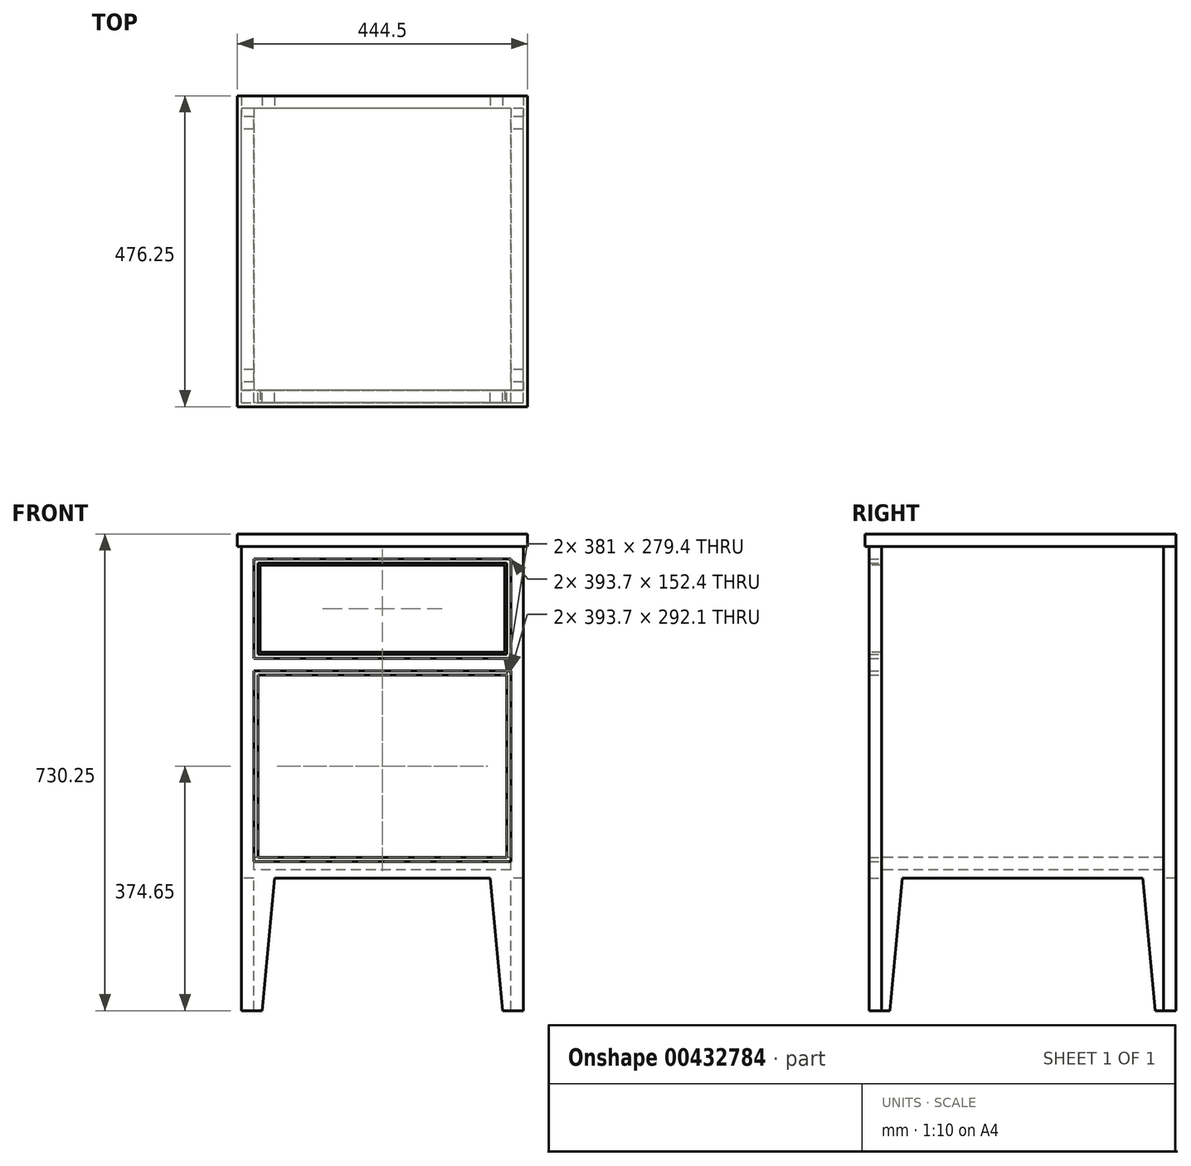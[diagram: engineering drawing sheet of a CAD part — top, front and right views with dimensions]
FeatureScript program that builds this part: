
annotation { "Feature Type Name" : "Feature", "Feature Type Description" : "" }
export const myFeature = defineFeature(function(context is Context, id is Id, definition is map)
    precondition{}
    {
        {
            var Q0;
            Q0=qCreatedBy(makeId("Front.planeOp"),FACE);
            var sketch = newSketch(context, id + "F0", { "sketchPlane" : qUnion([Q0])});
            skLineSegment(sketch, "E0.bottom", {"start": v(0, 0) * mm, "end": v(31.75, 0) * mm});
            skLineSegment(sketch, "E0.top", {"start": v(0, 711.2) * mm, "end": v(431.8, 711.2) * mm});
            skLineSegment(sketch, "E0.left", {"start": v(0, 0) * mm, "end": v(0, 711.2) * mm});
            skLineSegment(sketch, "E0.right", {"start": v(431.8, 0) * mm, "end": v(431.8, 711.2) * mm});
            skLineSegment(sketch, "E1", {"start": v(215.9, 711.2) * mm, "end": v(215.9, 0) * mm, "construction": true});
            skLineSegment(sketch, "E2.bottom", {"start": v(412.75, 539.75) * mm, "end": v(19.05, 539.75) * mm});
            skLineSegment(sketch, "E2.top", {"start": v(412.75, 692.15) * mm, "end": v(19.05, 692.15) * mm});
            skLineSegment(sketch, "E2.left", {"start": v(412.75, 539.75) * mm, "end": v(412.75, 692.15) * mm});
            skLineSegment(sketch, "E2.right", {"start": v(19.05, 539.75) * mm, "end": v(19.05, 692.15) * mm});
            skPoint(sketch, "E2.middle", {"position": v(215.9, 615.95) * mm});
            skLineSegment(sketch, "E3.bottom", {"start": v(412.75, 228.6) * mm, "end": v(19.05, 228.6) * mm});
            skLineSegment(sketch, "E3.top", {"start": v(412.75, 520.7) * mm, "end": v(19.05, 520.7) * mm});
            skLineSegment(sketch, "E3.left", {"start": v(412.75, 228.6) * mm, "end": v(412.75, 520.7) * mm});
            skLineSegment(sketch, "E3.right", {"start": v(19.05, 228.6) * mm, "end": v(19.05, 520.7) * mm});
            skPoint(sketch, "E3.middle", {"position": v(215.9, 374.65) * mm});
            skLineSegment(sketch, "E4", {"start": v(31.75, 0) * mm, "end": v(50.8, 203.2) * mm});
            skLineSegment(sketch, "E5", {"start": v(50.8, 203.2) * mm, "end": v(381, 203.2) * mm});
            skLineSegment(sketch, "E6", {"start": v(381, 203.2) * mm, "end": v(400.05, 0) * mm});
            skLineSegment(sketch, "E7.trimOffspring", {"start": v(400.05, 0) * mm, "end": v(431.8, 0) * mm});
            skSolve(sketch);
        }
        {
            var Q0;
            Q0 = qSketchRegion(id + "F0", true);
            extrude(context, id + "F1", {"entities" : qUnion([Q0]), "depth" : 19.05 * mm});
        }
        {
            var Q0;
            Q0=qCreatedBy(makeId("Front.planeOp"),FACE);
            var sketch = newSketch(context, id + "F2", { "sketchPlane" : qUnion([Q0])});
            skLineSegment(sketch, "E8.0", {"start": v(19.05, 228.6) * mm, "end": v(19.05, 520.7) * mm});
            skLineSegment(sketch, "E8.1", {"start": v(412.75, 520.7) * mm, "end": v(19.05, 520.7) * mm});
            skLineSegment(sketch, "E8.2", {"start": v(412.75, 228.6) * mm, "end": v(412.75, 520.7) * mm});
            skLineSegment(sketch, "E8.3", {"start": v(412.75, 228.6) * mm, "end": v(19.05, 228.6) * mm});
            skLineSegment(sketch, "E9.0", {"start": v(25.4, 234.95) * mm, "end": v(25.4, 514.35) * mm});
            skLineSegment(sketch, "E9.1", {"start": v(406.4, 234.95) * mm, "end": v(25.4, 234.95) * mm});
            skLineSegment(sketch, "E9.2", {"start": v(406.4, 234.95) * mm, "end": v(406.4, 514.35) * mm});
            skLineSegment(sketch, "E9.3", {"start": v(406.4, 514.35) * mm, "end": v(25.4, 514.35) * mm});
            skSolve(sketch);
        }
        {
            var Q0;
            Q0=makeQuery(id+"F2.imprint","IMPRINT",FACE,{"disambiguationData":[TD([[makeQuery(id+"F2.imprint","IMPRINT",EDGE,{"derivedFrom":sQuery(id+"F2.wireOp",EDGE,"E8.0")}),-1.0]])]});
            extrude(context, id + "F3", {"entities" : qUnion([Q0]), "depth" : 19.05 * mm});
        }
        {
            var Q0;
            Q0=qCreatedBy(makeId("Front.planeOp"),FACE);
            var sketch = newSketch(context, id + "F4", { "sketchPlane" : qUnion([Q0])});
            skLineSegment(sketch, "E10.0", {"start": v(412.75, 692.15) * mm, "end": v(19.05, 692.15) * mm});
            skLineSegment(sketch, "E10.1", {"start": v(19.05, 539.75) * mm, "end": v(19.05, 692.15) * mm});
            skLineSegment(sketch, "E10.2", {"start": v(412.75, 539.75) * mm, "end": v(19.05, 539.75) * mm});
            skLineSegment(sketch, "E10.3", {"start": v(412.75, 539.75) * mm, "end": v(412.75, 692.15) * mm});
            skLineSegment(sketch, "E11.0", {"start": v(406.4, 685.8) * mm, "end": v(25.4, 685.8) * mm});
            skLineSegment(sketch, "E11.1", {"start": v(406.4, 546.1) * mm, "end": v(406.4, 685.8) * mm});
            skLineSegment(sketch, "E11.2", {"start": v(406.4, 546.1) * mm, "end": v(25.4, 546.1) * mm});
            skLineSegment(sketch, "E11.3", {"start": v(25.4, 546.1) * mm, "end": v(25.4, 685.8) * mm});
            skSolve(sketch);
        }
        {
            var Q0;
            Q0=makeQuery(id+"F4.imprint","IMPRINT",FACE,{"disambiguationData":[TD([[makeQuery(id+"F4.imprint","IMPRINT",EDGE,{"derivedFrom":sQuery(id+"F4.wireOp",EDGE,"E10.0")}),1.0]])]});
            extrude(context, id + "F5", {"entities" : qUnion([Q0]), "depth" : 19.05 * mm});
        }
        {
            var Q0;
            Q0=qCreatedBy(makeId("Right.planeOp"),FACE);
            var sketch = newSketch(context, id + "F6", { "sketchPlane" : qUnion([Q0])});
            skLineSegment(sketch, "E12.0", {"start": v(0, 0) * mm, "end": v(0, 711.2) * mm});
            skLineSegment(sketch, "E13", {"start": v(0, 711.2) * mm, "end": v(431.8, 711.2) * mm});
            skLineSegment(sketch, "E14", {"start": v(431.8, 711.2) * mm, "end": v(431.8, 0) * mm});
            skLineSegment(sketch, "E15", {"start": v(431.8, 0) * mm, "end": v(419.1, 0) * mm});
            skLineSegment(sketch, "E16", {"start": v(12.7, 0) * mm, "end": v(31.75, 203.2) * mm});
            skLineSegment(sketch, "E17", {"start": v(31.75, 203.2) * mm, "end": v(400.05, 203.2) * mm});
            skLineSegment(sketch, "E18", {"start": v(400.05, 203.2) * mm, "end": v(419.1, 0) * mm});
            skLineSegment(sketch, "E19.trimOffspring", {"start": v(12.7, 0) * mm, "end": v(0, 0) * mm});
            skSolve(sketch);
        }
        {
            var Q0;
            Q0=makeQuery(id+"F6.imprint","IMPRINT",FACE,{"disambiguationData":[TD([[makeQuery(id+"F6.imprint","IMPRINT",EDGE,{"derivedFrom":sQuery(id+"F6.wireOp",EDGE,"E12.0")}),-1.0]])]});
            extrude(context, id + "F7", {"entities" : qUnion([Q0]), "depth" : 19.05 * mm});
        }
        {
            var Q0;
            Q0=makeQuery(id+"F7.opExtrude","SWEPT_FACE",FACE,{"disambiguationData":[OSD([sQuery(id+"F6.wireOp",EDGE,"E14")])]});
            var sketch = newSketch(context, id + "F8", { "sketchPlane" : qUnion([Q0])});
            skLineSegment(sketch, "E20.bottom", {"start": v(-431.8, 0) * mm, "end": v(-400.05, 0) * mm});
            skLineSegment(sketch, "E20.top", {"start": v(-431.8, 711.2) * mm, "end": v(0, 711.2) * mm});
            skLineSegment(sketch, "E20.left", {"start": v(-431.8, 0) * mm, "end": v(-431.8, 711.2) * mm});
            skLineSegment(sketch, "E20.right", {"start": v(0, 0) * mm, "end": v(0, 711.2) * mm});
            skLineSegment(sketch, "E21", {"start": v(-215.9, 711.2) * mm, "end": v(-215.9, 0) * mm, "construction": true});
            skPoint(sketch, "E22.middle", {"position": v(-215.9, 615.95) * mm});
            skPoint(sketch, "E23.middle", {"position": v(-215.9, 374.65) * mm});
            skLineSegment(sketch, "E24", {"start": v(-400.05, 0) * mm, "end": v(-381, 203.2) * mm});
            skLineSegment(sketch, "E25", {"start": v(-381, 203.2) * mm, "end": v(-50.8, 203.2) * mm});
            skLineSegment(sketch, "E26", {"start": v(-50.8, 203.2) * mm, "end": v(-31.75, 0) * mm});
            skLineSegment(sketch, "E27.trimOffspring", {"start": v(-31.75, 0) * mm, "end": v(0, 0) * mm});
            skLineSegment(sketch, "E28.0", {"start": v(0, 711.2) * mm, "end": v(0, 0) * mm});
            skSolve(sketch);
        }
        {
            var Q0;
            Q0 = qSketchRegion(id + "F8", true);
            extrude(context, id + "F9", {"entities" : qUnion([Q0]), "depth" : 19.05 * mm});
        }
        {
            var Q0;
            Q0=makeQuery(id+"F7.opExtrude","SWEPT_BODY",BODY,{"disambiguationData":[OSD([sQuery(id+"F6.wireOp",EDGE,"E12.0"),sQuery(id+"F6.wireOp",EDGE,"E13"),sQuery(id+"F6.wireOp",EDGE,"E14"),sQuery(id+"F6.wireOp",EDGE,"E15"),sQuery(id+"F6.wireOp",EDGE,"E16"),sQuery(id+"F6.wireOp",EDGE,"E17"),sQuery(id+"F6.wireOp",EDGE,"E18"),sQuery(id+"F6.wireOp",EDGE,"E19.trimOffspring")])]});
            transform(context, id + "F10", {"entities" : qUnion([Q0]), "transformType" : TransformType.TRANSLATION_3D, "dx" : 412.75 * mm, "dy" : 0 * mm, "dz" : 0 * mm, "makeCopy" : true});
        }
        {
            var Q0;
            Q0=makeQuery(id+"F7.opExtrude","SWEPT_FACE",FACE,{"disambiguationData":[OSD([sQuery(id+"F6.wireOp",EDGE,"E13")])]});
            var sketch = newSketch(context, id + "F11", { "sketchPlane" : qUnion([Q0])});
            skLineSegment(sketch, "E29.1", {"start": v(0, -19.05) * mm, "end": v(431.8, -19.05) * mm});
            skLineSegment(sketch, "E30.0", {"start": v(438.15, 450.85) * mm, "end": v(-6.35, 450.85) * mm});
            skLineSegment(sketch, "E31.0", {"start": v(-6.35, -25.4) * mm, "end": v(-6.35, 450.85) * mm});
            skLineSegment(sketch, "E32.0", {"start": v(-6.35, -25.4) * mm, "end": v(438.15, -25.4) * mm});
            skLineSegment(sketch, "E33.0", {"start": v(438.15, -25.4) * mm, "end": v(438.15, 450.85) * mm});
            skPoint(sketch, "E34.orphan", {"position": v(0, 450.85) * mm});
            skPoint(sketch, "E35.orphan", {"position": v(431.8, 450.85) * mm});
            skSolve(sketch);
        }
        {
            var Q0;
            Q0 = qSketchRegion(id + "F11", true);
            extrude(context, id + "F12", {"entities" : qUnion([Q0]), "depth" : 19.05 * mm});
        }
        {
            var Q0;
            Q0=makeQuery(id+"F1.opExtrude","CAP_FACE",FACE,{"disambiguationData":[OSD([sQuery(id+"F0.wireOp",EDGE,"E0.bottom"),sQuery(id+"F0.wireOp",EDGE,"E0.top"),sQuery(id+"F0.wireOp",EDGE,"E0.left"),sQuery(id+"F0.wireOp",EDGE,"E0.right"),sQuery(id+"F0.wireOp",EDGE,"E2.bottom"),sQuery(id+"F0.wireOp",EDGE,"E2.top"),sQuery(id+"F0.wireOp",EDGE,"E2.left"),sQuery(id+"F0.wireOp",EDGE,"E2.right"),sQuery(id+"F0.wireOp",EDGE,"E3.bottom"),sQuery(id+"F0.wireOp",EDGE,"E3.top"),sQuery(id+"F0.wireOp",EDGE,"E3.left"),sQuery(id+"F0.wireOp",EDGE,"E3.right"),sQuery(id+"F0.wireOp",EDGE,"E4"),sQuery(id+"F0.wireOp",EDGE,"E5"),sQuery(id+"F0.wireOp",EDGE,"E6"),sQuery(id+"F0.wireOp",EDGE,"E7.trimOffspring")])],"isStart":true});
            var sketch = newSketch(context, id + "F13", { "sketchPlane" : qUnion([Q0])});
            skLineSegment(sketch, "E36.0", {"start": v(-412.75, 215.9) * mm, "end": v(-412.75, 234.95) * mm});
            skLineSegment(sketch, "E36.1", {"start": v(-19.05, 215.9) * mm, "end": v(-19.05, 234.95) * mm});
            skLineSegment(sketch, "E36.2", {"start": v(-412.75, 234.95) * mm, "end": v(-19.05, 234.95) * mm});
            skPoint(sketch, "E37.orphan", {"position": v(-406.4, 234.95) * mm});
            skPoint(sketch, "E38.orphan", {"position": v(-25.4, 234.95) * mm});
            skLineSegment(sketch, "E39.0", {"start": v(-412.75, 215.9) * mm, "end": v(-19.05, 215.9) * mm});
            skPoint(sketch, "E40.orphan", {"position": v(-412.75, 711.2) * mm});
            skPoint(sketch, "E41.orphan", {"position": v(-412.75, 0) * mm});
            skPoint(sketch, "E42.orphan", {"position": v(-19.05, 0) * mm});
            skPoint(sketch, "E43.orphan", {"position": v(-19.05, 711.2) * mm});
            skSolve(sketch);
        }
        {
            var Q0;
            Q0 = qSketchRegion(id + "F13", true);
            var Q1;
            Q1=makeQuery(id+"F10.opPattern","COPY",FACE,{"derivedFrom":makeQuery(id+"F7.opExtrude","SWEPT_FACE",FACE,{"disambiguationData":[OSD([sQuery(id+"F6.wireOp",EDGE,"E14")])]}),"instanceName":"1"});
            extrude(context, id + "F14", {"entities" : qUnion([Q0]), "endBound" : BoundingType.UP_TO_SURFACE, "endBoundEntityFace" : qUnion([Q1]), "depth" : 25.4 * mm});
        }
        {
            var Q0;
            Q0=makeQuery(id+"F1.opExtrude","CAP_FACE",FACE,{"disambiguationData":[OSD([sQuery(id+"F0.wireOp",EDGE,"E0.bottom"),sQuery(id+"F0.wireOp",EDGE,"E0.top"),sQuery(id+"F0.wireOp",EDGE,"E0.left"),sQuery(id+"F0.wireOp",EDGE,"E0.right"),sQuery(id+"F0.wireOp",EDGE,"E2.bottom"),sQuery(id+"F0.wireOp",EDGE,"E2.top"),sQuery(id+"F0.wireOp",EDGE,"E2.left"),sQuery(id+"F0.wireOp",EDGE,"E2.right"),sQuery(id+"F0.wireOp",EDGE,"E3.bottom"),sQuery(id+"F0.wireOp",EDGE,"E3.top"),sQuery(id+"F0.wireOp",EDGE,"E3.left"),sQuery(id+"F0.wireOp",EDGE,"E3.right"),sQuery(id+"F0.wireOp",EDGE,"E4"),sQuery(id+"F0.wireOp",EDGE,"E5"),sQuery(id+"F0.wireOp",EDGE,"E6"),sQuery(id+"F0.wireOp",EDGE,"E7.trimOffspring")])],"isStart":false});
            var sketch = newSketch(context, id + "F15", { "sketchPlane" : qUnion([Q0])});
            skLineSegment(sketch, "E44.0", {"start": v(403.23, 549.27) * mm, "end": v(28.57, 549.27) * mm});
            skLineSegment(sketch, "E44.1", {"start": v(403.23, 549.27) * mm, "end": v(403.23, 682.63) * mm});
            skLineSegment(sketch, "E44.2", {"start": v(403.23, 682.63) * mm, "end": v(28.57, 682.63) * mm});
            skLineSegment(sketch, "E44.3", {"start": v(28.57, 549.27) * mm, "end": v(28.57, 682.63) * mm});
            skSolve(sketch);
        }
        {
            var Q0;
            Q0 = qSketchRegion(id + "F15", true);
            extrude(context, id + "F16", {"entities" : qUnion([Q0]), "oppositeDirection" : true, "depth" : 19.05 * mm});
        }
    });
